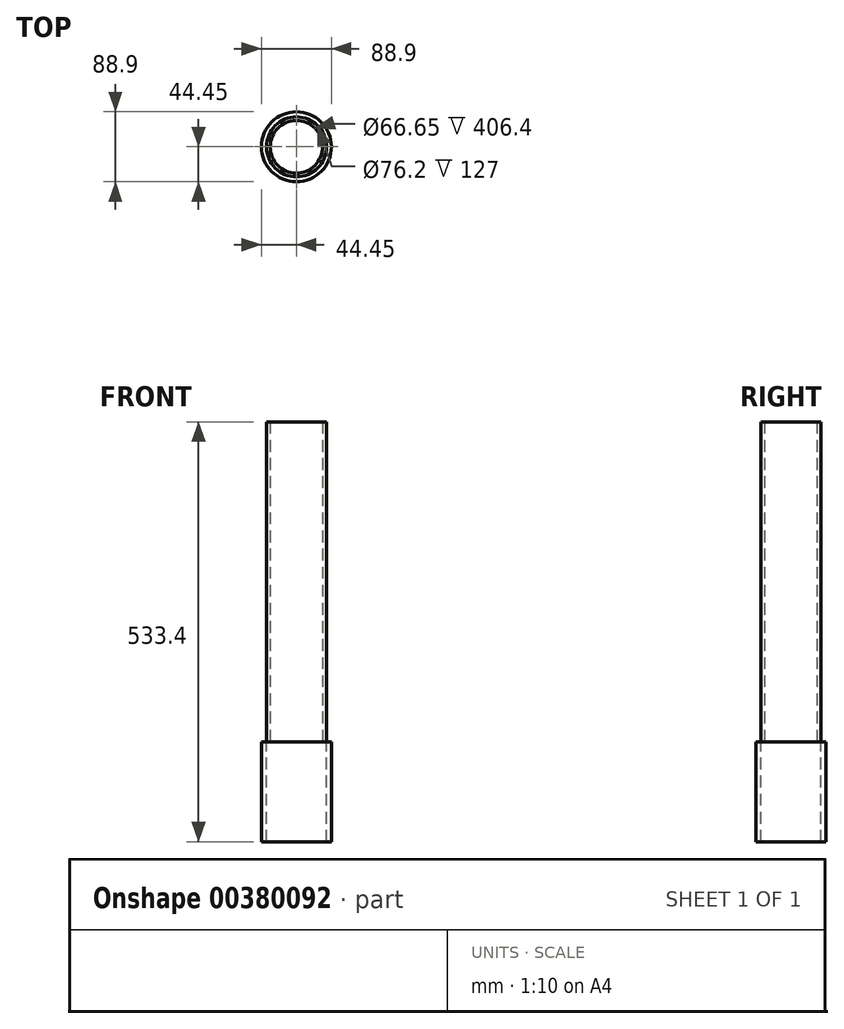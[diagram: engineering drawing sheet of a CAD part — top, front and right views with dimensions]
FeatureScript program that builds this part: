
annotation { "Feature Type Name" : "Feature", "Feature Type Description" : "" }
export const myFeature = defineFeature(function(context is Context, id is Id, definition is map)
    precondition{}
    {
        {
            var Q0;
            Q0=qCreatedBy(makeId("Top.planeOp"),FACE);
            var sketch = newSketch(context, id + "F0", { "sketchPlane" : qUnion([Q0])});
            skCircle(sketch, "E0", {"center": v(0, 0) * mm, "radius": 44.45 * mm});
            skCircle(sketch, "E1", {"center": v(0, 0) * mm, "radius": 38.1 * mm});
            skSolve(sketch);
        }
        {
            var Q0;
            Q0=makeQuery(id+"F0.imprint","IMPRINT",FACE,{"disambiguationData":[TD([[makeQuery(id+"F0.imprint","IMPRINT",EDGE,{"derivedFrom":sQuery(id+"F0.wireOp",EDGE,"E0")}),1.0]])]});
            extrude(context, id + "F1", {"entities" : qUnion([Q0]), "oppositeDirection" : true, "depth" : 127 * mm});
        }
        {
            var Q0;
            Q0=qCreatedBy(makeId("Top.planeOp"),FACE);
            var sketch = newSketch(context, id + "F2", { "sketchPlane" : qUnion([Q0])});
            skCircle(sketch, "E2", {"center": v(0, 0) * mm, "radius": 38.1 * mm});
            skCircle(sketch, "E3", {"center": v(0, 0) * mm, "radius": 33.32 * mm});
            skSolve(sketch);
        }
        {
            var Q0;
            Q0=qSketchRegion(id+"F2",true);
            extrude(context, id + "F3", {"entities" : qUnion([Q0]), "depth" : 406.4 * mm});
        }
    });
